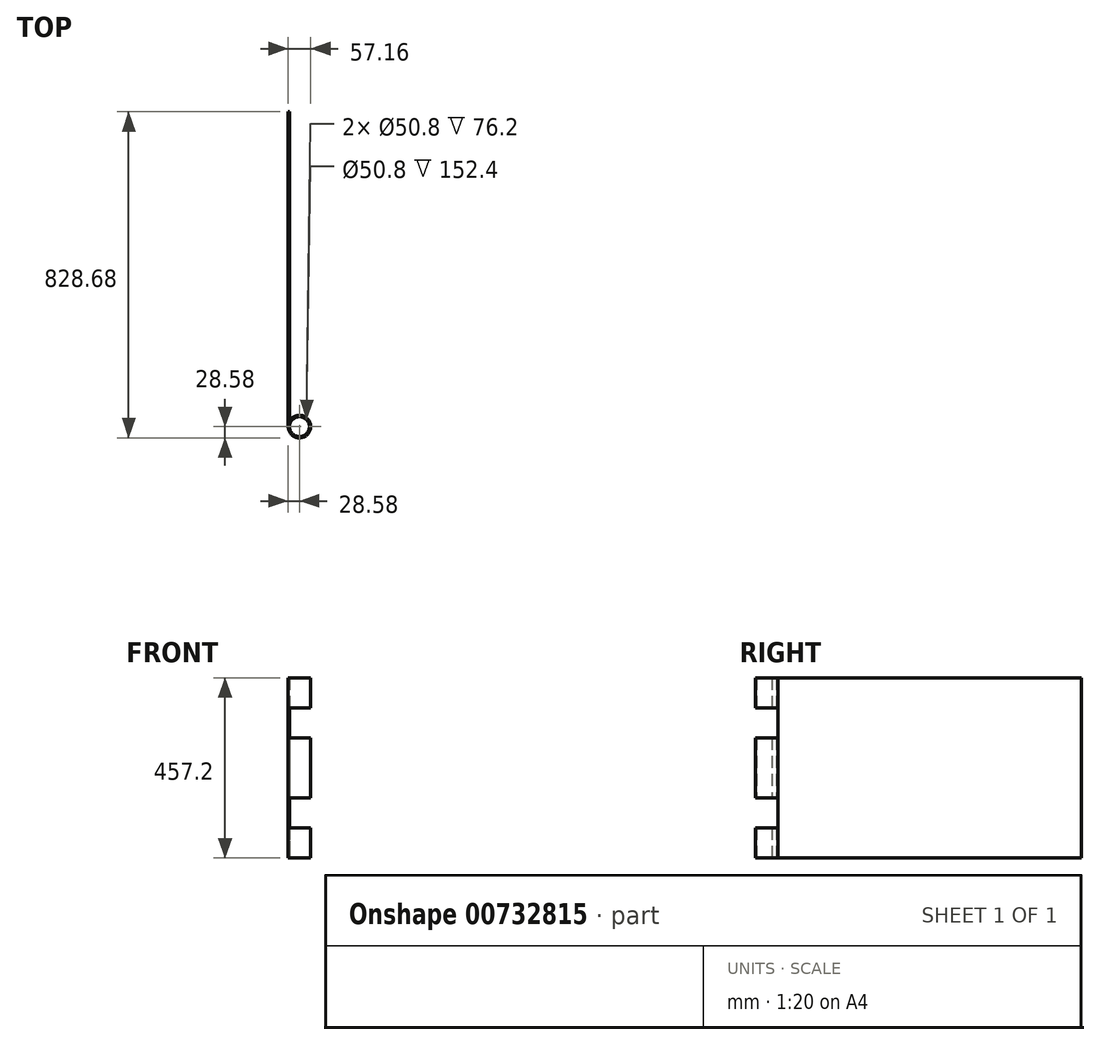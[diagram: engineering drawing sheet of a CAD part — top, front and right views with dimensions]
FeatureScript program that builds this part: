
annotation { "Feature Type Name" : "Feature", "Feature Type Description" : "" }
export const myFeature = defineFeature(function(context is Context, id is Id, definition is map)
    precondition{}
    {
        {
            var Q0;
            Q0=qCreatedBy(makeId("Top.planeOp"),FACE);
            var sketch = newSketch(context, id + "F0", { "sketchPlane" : qUnion([Q0])});
            skCircle(sketch, "E0", {"center": v(0, 0) * mm, "radius": 25.4 * mm});
            skArc(sketch, "E1.0", {"start": v(-28.58, 0) * mm, "mid": v(27.77, -6.74) * mm, "end": v(-25.4, 13.1) * mm});
            skLineSegment(sketch, "E2.top", {"start": v(-28.58, 800.1) * mm, "end": v(-25.4, 800.1) * mm});
            skLineSegment(sketch, "E2.left", {"start": v(-28.58, 0) * mm, "end": v(-28.58, 800.1) * mm});
            skLineSegment(sketch, "E2.right", {"start": v(-25.4, 13.1) * mm, "end": v(-25.4, 800.1) * mm});
            skSolve(sketch);
        }
        {
            var Q0;
            Q0 = qSketchRegion(id + "F0", true);
            extrude(context, id + "F1", {"entities" : qUnion([Q0]), "depth" : 457.2 * mm, "offsetDistance" : 25.4 * mm});
        }
        {
            var Q0;
            Q0=qCreatedBy(makeId("Right.planeOp"),FACE);
            var sketch = newSketch(context, id + "F2", { "sketchPlane" : qUnion([Q0])});
            skLineSegment(sketch, "E3.bottom", {"start": v(28.57, 381) * mm, "end": v(-28.58, 381) * mm});
            skLineSegment(sketch, "E3.top", {"start": v(28.57, 304.8) * mm, "end": v(-28.58, 304.8) * mm});
            skLineSegment(sketch, "E3.left", {"start": v(28.57, 381) * mm, "end": v(28.57, 304.8) * mm});
            skLineSegment(sketch, "E3.right", {"start": v(-28.58, 381) * mm, "end": v(-28.58, 304.8) * mm});
            skPoint(sketch, "E3.middle", {"position": v(0, 342.9) * mm});
            skLineSegment(sketch, "E4.bottom", {"start": v(28.57, 152.4) * mm, "end": v(-28.57, 152.4) * mm});
            skLineSegment(sketch, "E4.top", {"start": v(28.57, 76.2) * mm, "end": v(-28.58, 76.2) * mm});
            skLineSegment(sketch, "E4.left", {"start": v(28.57, 152.4) * mm, "end": v(28.57, 76.2) * mm});
            skLineSegment(sketch, "E4.right", {"start": v(-28.58, 152.4) * mm, "end": v(-28.58, 76.2) * mm});
            skPoint(sketch, "E4.middle", {"position": v(0, 114.3) * mm});
            skSolve(sketch);
        }
        {
            var Q0;
            Q0 = qSketchRegion(id + "F2", true);
            extrude(context, id + "F3", {"entities" : qUnion([Q0]), "operationType" : NewBodyOperationType.REMOVE, "endBound" : BoundingType.THROUGH_ALL, "oppositeDirection" : true, "depth" : 25.4 * mm, "offsetDistance" : 25.4 * mm, "hasSecondDirection" : true, "secondDirectionBound" : BoundingType.THROUGH_ALL, "secondDirectionOppositeDirection" : false, "secondDirectionDepth" : 25.4 * mm});
        }
    });
